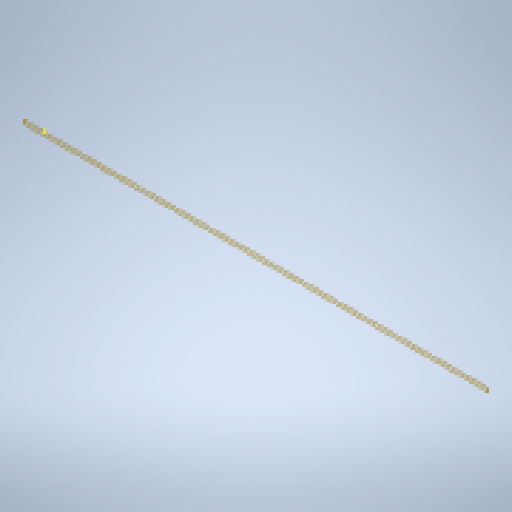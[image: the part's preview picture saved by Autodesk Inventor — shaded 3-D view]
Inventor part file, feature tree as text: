
AUTODESK INVENTOR PART (.ipt)
format: ipt  version: 2024.2 (Build 282272000, 272)  size: 118,272 bytes
history: native  units: mm
features: other x5, extrude x1, sketch x1
ambient origin geometry x8: Origin, YZ Plane, XZ Plane, XY Plane, X Axis, Y Axis, Z Axis, Center Point
bodies: Body1 (feature_tree)
feature tree (7):
  other  "Твердое тело1"
  other  "РабПлоскость1"
  extrude  "Выдавливание1"  Depth=10.0mm TaperAngle=0.0deg
  sketch  "Эскиз1"
  parser-record x1  (decoder bookkeeping rows leaked as tree rows — omitted from the tree; the rows remain in map.json)
  other  "полигон етз.iam"
  other  "брусок:1"
note: 1 file-system path scrubbed to <path> (originals preserved in map.json)
